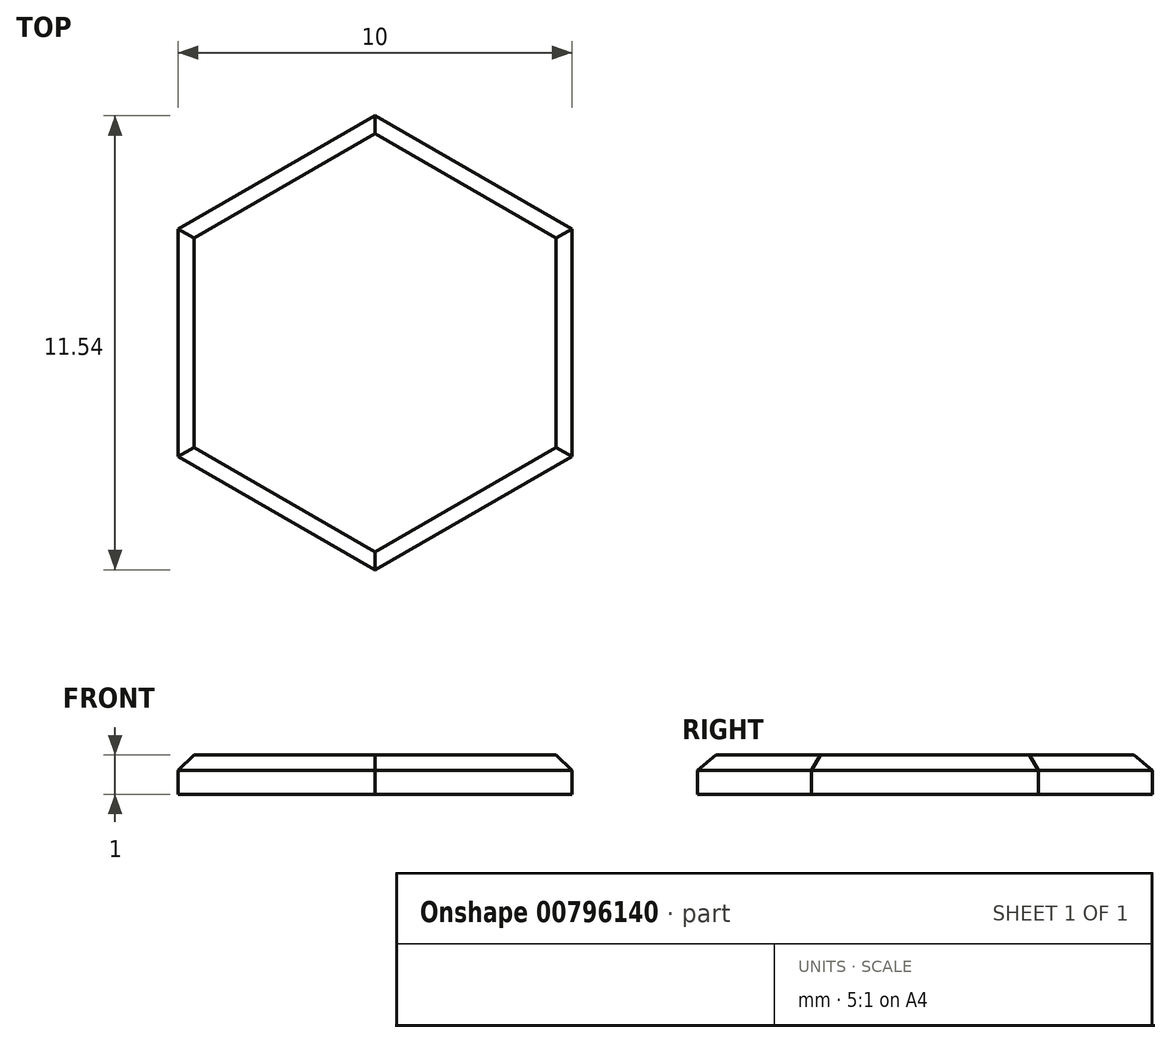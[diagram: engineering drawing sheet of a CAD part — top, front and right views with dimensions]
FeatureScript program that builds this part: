
annotation { "Feature Type Name" : "Feature", "Feature Type Description" : "" }
export const myFeature = defineFeature(function(context is Context, id is Id, definition is map)
    precondition{}
    {
        {
            var Q0;
            Q0=qCreatedBy(makeId("Top.planeOp"),FACE);
            var sketch = newSketch(context, id + "F0", { "sketchPlane" : qUnion([Q0])});
            skCircle(sketch, "E0.cCircle", {"center": v(0, 0) * mm, "radius": 5 * mm, "construction": true});
            skLineSegment(sketch, "E0.0", {"start": v(5, 2.89) * mm, "end": v(5, -2.89) * mm});
            skLineSegment(sketch, "E0.1", {"start": v(5, -2.89) * mm, "end": v(0, -5.77) * mm});
            skLineSegment(sketch, "E0.2", {"start": v(0, -5.77) * mm, "end": v(-5, -2.89) * mm});
            skLineSegment(sketch, "E0.3", {"start": v(-5, -2.89) * mm, "end": v(-5, 2.89) * mm});
            skLineSegment(sketch, "E0.4", {"start": v(-5, 2.89) * mm, "end": v(0, 5.77) * mm});
            skLineSegment(sketch, "E0.5", {"start": v(0, 5.77) * mm, "end": v(5, 2.89) * mm});
            skPoint(sketch, "E0.0.midPoint", {"position": v(5, 0) * mm});
            skSolve(sketch);
        }
        {
            var Q0;
            Q0=makeQuery(id+"F0.imprint","IMPRINT",FACE,{"disambiguationData":[TD([[makeQuery(id+"F0.imprint","IMPRINT",EDGE,{"derivedFrom":sQuery(id+"F0.wireOp",EDGE,"E0.0")}),-1.0]])]});
            extrude(context, id + "F1", {"entities" : qUnion([Q0]), "depth" : 1 * mm, "offsetDistance" : 25 * mm});
        }
        {
            var Q0;
            Q0=makeQuery(id+"F1.opExtrude","CAP_EDGE",EDGE,{"disambiguationData":[OSD([sQuery(id+"F0.wireOp",EDGE,"E0.2")])],"isStart":false});
            var Q1;
            Q1=makeQuery(id+"F1.opExtrude","CAP_EDGE",EDGE,{"disambiguationData":[OSD([sQuery(id+"F0.wireOp",EDGE,"E0.3")])],"isStart":false});
            var Q2;
            Q2=makeQuery(id+"F1.opExtrude","CAP_EDGE",EDGE,{"disambiguationData":[OSD([sQuery(id+"F0.wireOp",EDGE,"E0.4")])],"isStart":false});
            var Q3;
            Q3=makeQuery(id+"F1.opExtrude","CAP_EDGE",EDGE,{"disambiguationData":[OSD([sQuery(id+"F0.wireOp",EDGE,"E0.5")])],"isStart":false});
            var Q4;
            Q4=makeQuery(id+"F1.opExtrude","CAP_EDGE",EDGE,{"disambiguationData":[OSD([sQuery(id+"F0.wireOp",EDGE,"E0.0")])],"isStart":false});
            var Q5;
            Q5=makeQuery(id+"F1.opExtrude","CAP_EDGE",EDGE,{"disambiguationData":[OSD([sQuery(id+"F0.wireOp",EDGE,"E0.1")])],"isStart":false});
            chamfer(context, id + "F2", {"entities" : qUnion([Q0, Q1, Q2, Q3, Q4, Q5]), "width" : 0.4 * mm, "tangentPropagation" : true});
        }
    });
